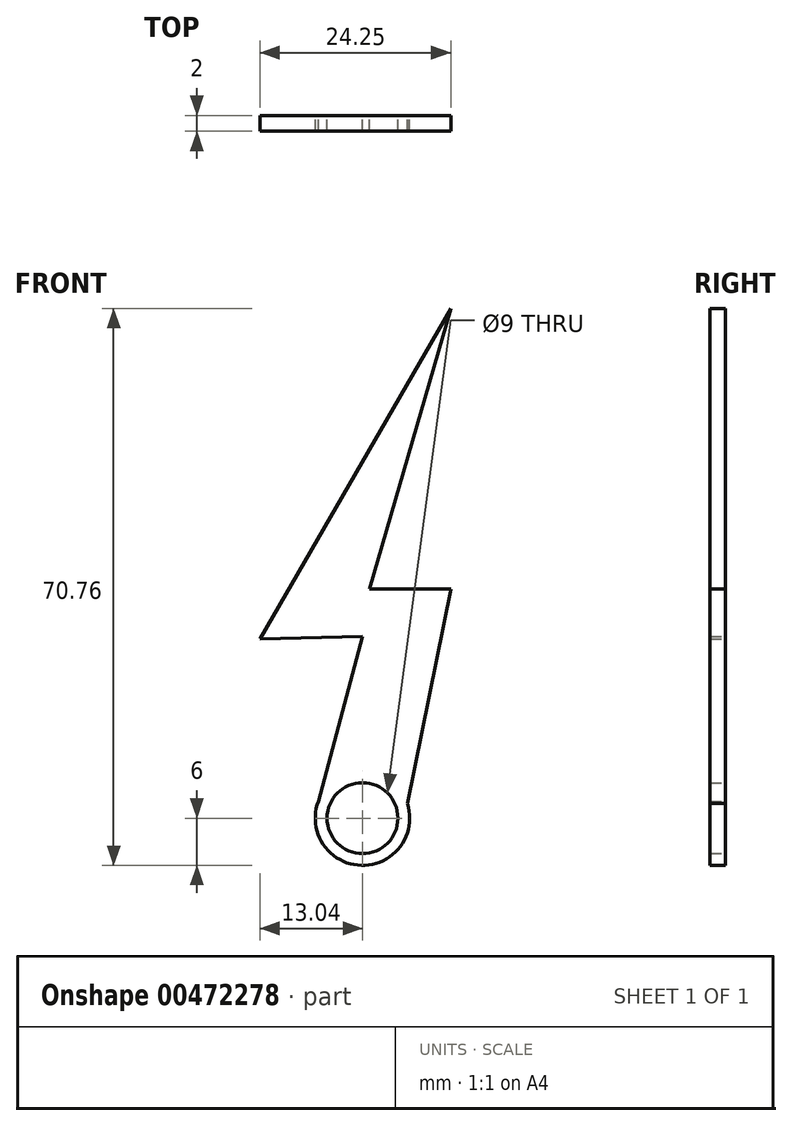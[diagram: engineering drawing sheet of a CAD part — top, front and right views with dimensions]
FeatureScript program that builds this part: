
annotation { "Feature Type Name" : "Feature", "Feature Type Description" : "" }
export const myFeature = defineFeature(function(context is Context, id is Id, definition is map)
    precondition{}
    {
        {
            var Q0;
            Q0=qCreatedBy(makeId("Front.planeOp"),FACE);
            var sketch = newSketch(context, id + "F0", { "sketchPlane" : qUnion([Q0])});
            skArc(sketch, "E0", {"start": v(-5.6, 2.14) * mm, "mid": v(-0.15, -6) * mm, "end": v(5.7, 1.86) * mm});
            skCircle(sketch, "E1", {"center": v(0, 0) * mm, "radius": 4.5 * mm});
            skLineSegment(sketch, "E2", {"start": v(-5.6, 2.14) * mm, "end": v(0, 23.07) * mm});
            skLineSegment(sketch, "E3", {"start": v(5.7, 1.86) * mm, "end": v(11.21, 29.14) * mm});
            skLineSegment(sketch, "E4", {"start": v(11.21, 29.14) * mm, "end": v(0.91, 29.14) * mm});
            skLineSegment(sketch, "E5", {"start": v(0.91, 29.14) * mm, "end": v(11.21, 64.76) * mm});
            skLineSegment(sketch, "E6", {"start": v(11.21, 64.76) * mm, "end": v(-13.04, 22.8) * mm});
            skLineSegment(sketch, "E7", {"start": v(-13.04, 22.8) * mm, "end": v(0, 23.07) * mm});
            skSolve(sketch);
        }
        {
            var Q0;
            Q0=makeQuery(id+"F0.imprint","IMPRINT",FACE,{"disambiguationData":[TD([[makeQuery(id+"F0.imprint","IMPRINT",EDGE,{"derivedFrom":sQuery(id+"F0.wireOp",EDGE,"E0")}),1.0]])]});
            extrude(context, id + "F1", {"entities" : qUnion([Q0]), "depth" : 2 * mm, "offsetDistance" : 25 * mm});
        }
    });
